# Revit family: T300298x
name_source: partatom
category: Furniture
revit_build: Autodesk Revit Architecture 2015 (Build: 20140322_1515(x64)
units: mm (PartAtom-declared; Revit-internal decimal feet)

## types (1)
- T300298
    Assembly Code = E2020400
    Catalog = https://ofs.com
    Coact End Table Leg Antiscratch = OFS COACT Modular Lounge - Black plastic
    Coact End Table Legs = OFS COACT Modular Lounge - Metal
    Coact End Table Outlet = OFS COACT Modular Lounge - White Plastic
    Coact End Table Table Material = OFS COACT Modular Lounge - Wood Table
    Coact Lounge Chair Armrest = OFS COACT Modular Lounge - Seat Support Fabric
    Coact Lounge Chair Back Shelf = OFS COACT Modular Lounge - Wood Table
    Coact Lounge Chair Brackets = OFS COACT Modular Lounge - Metal
    Coact Lounge Chair Cushion = OFS COACT Modular Lounge - Cushion Fabric
    Coact Lounge Chair Legs Antiscratch = OFS COACT Modular Lounge - Black plastic
    Coact Lounge Chair Outlet = OFS COACT Modular Lounge - White Plastic
    Coact Lounge Chair Seat Support = OFS COACT Modular Lounge - Seat Support Fabric
    Coact Lounge Chair Table = OFS COACT Modular Lounge - Wood Table
    Coact Lounge Chair Table Support = OFS COACT Modular Lounge - Metal
    Coact Lounge Chair legs = OFS COACT Modular Lounge - Metal
    Description = OFS TYPICAL T300298
    Manufacturer = OFS
    Model = T300298
    URL = https://ofs.com

## geometry (parser evidence)
native form markers: Sweep x12
no freeform markers — native parametric forms only
